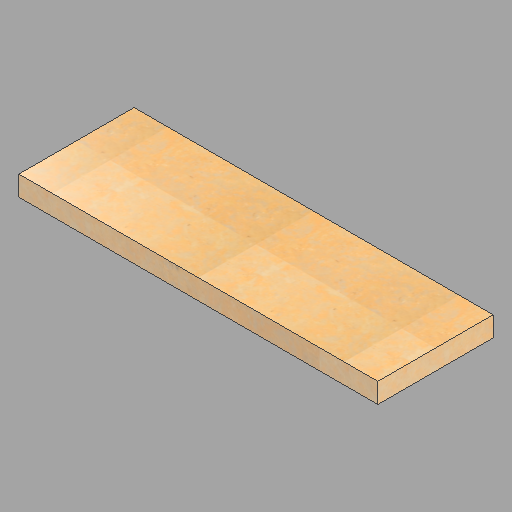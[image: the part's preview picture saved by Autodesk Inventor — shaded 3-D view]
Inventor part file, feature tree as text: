
AUTODESK INVENTOR PART (.ipt)
format: ipt  version: 2023 (Build 270158000, 158)  size: 218,624 bytes
history: native  units: in
note: dims shown in document units (in); Inventor stores cm internally (conversion verified against a paired STEP export)
features: extrude x1, sketch x1
ambient origin geometry x8: Origin, YZ Plane, XZ Plane, XY Plane, X Axis, Y Axis, Z Axis, Center Point
bodies: Solid1 (feature_tree)
feature tree (2):
  extrude  "Extrusion1"  Depth=23.0in
  sketch  "Sketch1"  dims[d0=71.625in d1=23.0in d2=4.0in d3=0.0in]
